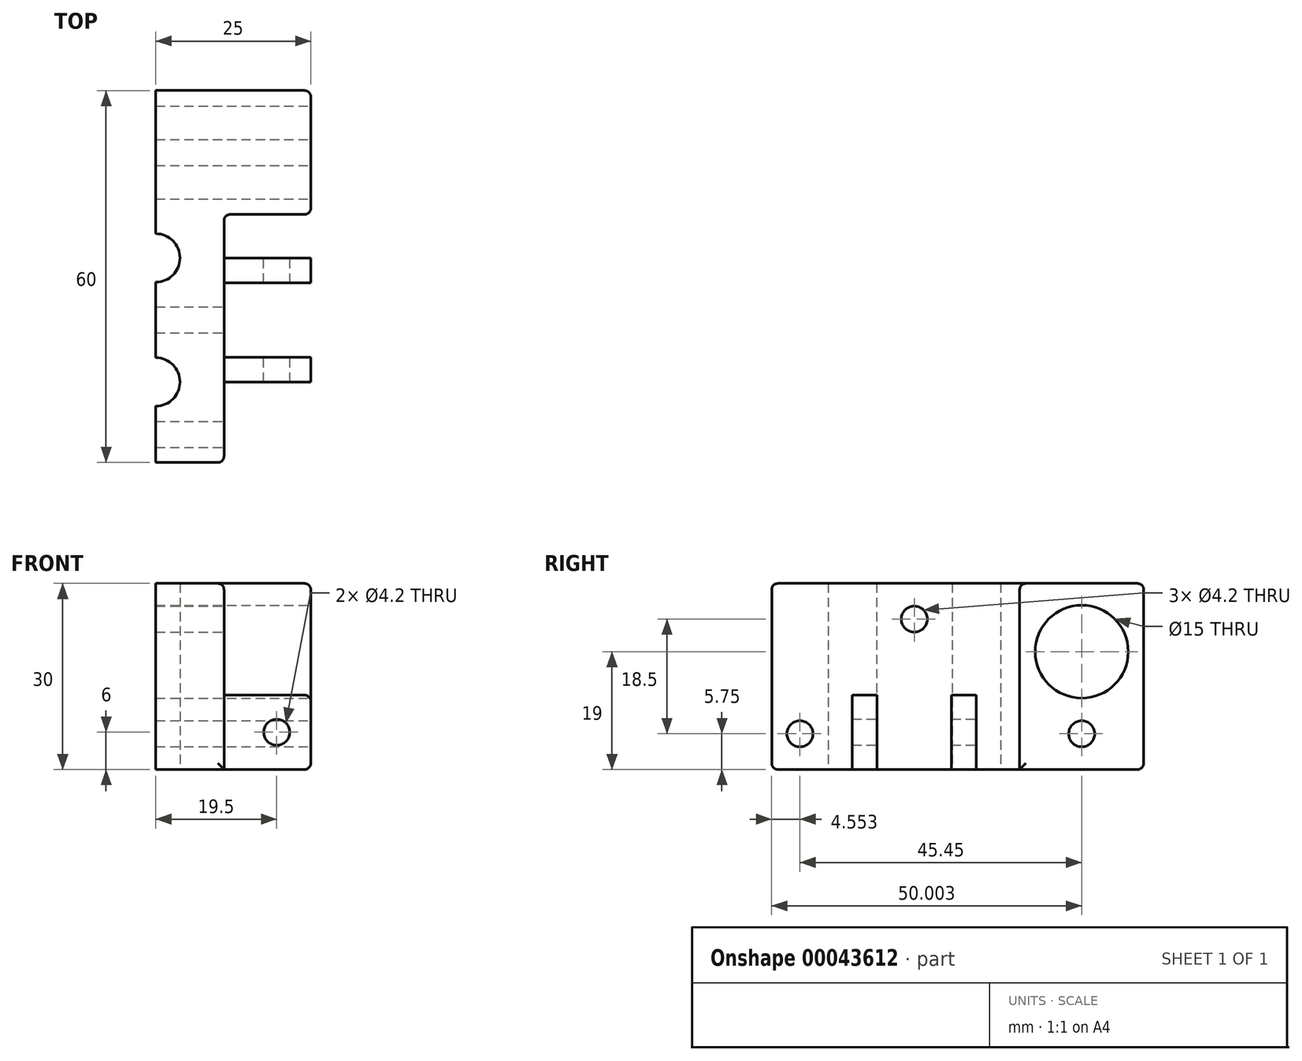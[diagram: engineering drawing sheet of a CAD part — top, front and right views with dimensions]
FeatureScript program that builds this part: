
annotation { "Feature Type Name" : "Feature", "Feature Type Description" : "" }
export const myFeature = defineFeature(function(context is Context, id is Id, definition is map)
    precondition{}
    {
        {
            var Q0;
            Q0=qCreatedBy(makeId("Top.planeOp"),FACE);
            var sketch = newSketch(context, id + "F0", { "sketchPlane" : qUnion([Q0])});
            skLineSegment(sketch, "E0.bottom", {"start": v(-39.71, 64.35) * mm, "end": v(-28.71, 64.35) * mm});
            skLineSegment(sketch, "E0.top", {"start": v(-39.71, 4.35) * mm, "end": v(-28.71, 4.35) * mm});
            skLineSegment(sketch, "E0.left", {"start": v(-39.71, 64.35) * mm, "end": v(-39.71, 4.35) * mm});
            skLineSegment(sketch, "E0.right", {"start": v(-28.71, 64.35) * mm, "end": v(-28.71, 4.35) * mm});
            skCircle(sketch, "E1", {"center": v(-39.71, 37.35) * mm, "radius": 3.9 * mm});
            skCircle(sketch, "E2", {"center": v(-39.71, 17.35) * mm, "radius": 3.9 * mm});
            skLineSegment(sketch, "E3.bottom", {"start": v(-28.71, 44.35) * mm, "end": v(-14.71, 44.35) * mm});
            skLineSegment(sketch, "E3.top", {"start": v(-28.71, 64.35) * mm, "end": v(-14.71, 64.35) * mm});
            skLineSegment(sketch, "E3.left", {"start": v(-28.71, 44.35) * mm, "end": v(-28.71, 64.35) * mm});
            skLineSegment(sketch, "E3.right", {"start": v(-14.71, 44.35) * mm, "end": v(-14.71, 64.35) * mm});
            skLineSegment(sketch, "E4.bottom", {"start": v(-28.71, 33.35) * mm, "end": v(-14.71, 33.35) * mm});
            skLineSegment(sketch, "E4.top", {"start": v(-28.71, 37.35) * mm, "end": v(-14.71, 37.35) * mm});
            skLineSegment(sketch, "E4.left", {"start": v(-28.71, 37.35) * mm, "end": v(-28.71, 33.35) * mm});
            skLineSegment(sketch, "E4.right", {"start": v(-14.71, 37.35) * mm, "end": v(-14.71, 33.35) * mm});
            skLineSegment(sketch, "E5.bottom", {"start": v(-28.71, 17.35) * mm, "end": v(-14.71, 17.35) * mm});
            skLineSegment(sketch, "E5.top", {"start": v(-28.71, 21.35) * mm, "end": v(-14.71, 21.35) * mm});
            skLineSegment(sketch, "E5.left", {"start": v(-28.71, 17.35) * mm, "end": v(-28.71, 21.35) * mm});
            skLineSegment(sketch, "E5.right", {"start": v(-14.71, 17.35) * mm, "end": v(-14.71, 21.35) * mm});
            skPoint(sketch, "E6", {"position": v(-39.71, 27.35) * mm});
            skPoint(sketch, "E7", {"position": v(-39.71, 8.9) * mm});
            skSolve(sketch);
        }
        {
            var Q0;
            {var subQ7=sQuery(id+"F0.wireOp",EDGE,"E0.bottom");Q0=makeQuery(id+"F0.imprint","IMPRINT",FACE,{"disambiguationData":[TD([[makeQuery(id+"F0.imprint","IMPRINT",EDGE,{"derivedFrom":subQ7}),-1.0]])]});}
            var Q1;
            Q1=makeQuery(id+"F0.imprint","IMPRINT",FACE,{"disambiguationData":[TD([[makeQuery(id+"F0.imprint","IMPRINT",EDGE,{"derivedFrom":sQuery(id+"F0.wireOp",EDGE,"E3.bottom")}),1.0]])]});
            extrude(context, id + "F1", {"entities" : qUnion([Q0, Q1]), "depth" : 30 * mm});
        }
        {
            var Q0;
            Q0=makeQuery(id+"F0.imprint","IMPRINT",FACE,{"disambiguationData":[TD([[makeQuery(id+"F0.imprint","IMPRINT",EDGE,{"derivedFrom":sQuery(id+"F0.wireOp",EDGE,"E4.bottom")}),1.0]])]});
            var Q1;
            Q1=makeQuery(id+"F0.imprint","IMPRINT",FACE,{"disambiguationData":[TD([[makeQuery(id+"F0.imprint","IMPRINT",EDGE,{"derivedFrom":sQuery(id+"F0.wireOp",EDGE,"E5.bottom")}),1.0]])]});
            extrude(context, id + "F2", {"entities" : qUnion([Q0, Q1]), "operationType" : NewBodyOperationType.ADD, "depth" : 12 * mm});
        }
        {
            var Q0;
            Q0=makeQuery(id+"F1.opExtrude","SWEPT_FACE",FACE,{"disambiguationData":[OSD([sQuery(id+"F0.wireOp",EDGE,"E3.right")])]});
            var sketch = newSketch(context, id + "F3", { "sketchPlane" : qUnion([Q0])});
            skCircle(sketch, "E8", {"center": v(54.35, 19) * mm, "radius": 7.5 * mm});
            skCircle(sketch, "E9", {"center": v(54.35, 5.75) * mm, "radius": 2.1 * mm});
            skCircle(sketch, "E10", {"center": v(8.9, 5.75) * mm, "radius": 2.1 * mm});
            skCircle(sketch, "E11", {"center": v(27.35, 24.25) * mm, "radius": 2.1 * mm});
            skSolve(sketch);
        }
        {
            var Q0;
            Q0=makeQuery(id+"F3.imprint","IMPRINT",FACE,{"disambiguationData":[TD([[makeQuery(id+"F3.imprint","IMPRINT",EDGE,{"derivedFrom":sQuery(id+"F3.wireOp",EDGE,"E8")}),1.0]])]});
            var Q1;
            Q1=makeQuery(id+"F3.imprint","IMPRINT",FACE,{"disambiguationData":[TD([[makeQuery(id+"F3.imprint","IMPRINT",EDGE,{"derivedFrom":sQuery(id+"F3.wireOp",EDGE,"E9")}),1.0]])]});
            var Q2;
            Q2=makeQuery(id+"F3.imprint","IMPRINT",FACE,{"disambiguationData":[TD([[makeQuery(id+"F3.imprint","IMPRINT",EDGE,{"derivedFrom":sQuery(id+"F3.wireOp",EDGE,"E11")}),1.0]])]});
            var Q3;
            Q3=makeQuery(id+"F3.imprint","IMPRINT",FACE,{"disambiguationData":[TD([[makeQuery(id+"F3.imprint","IMPRINT",EDGE,{"derivedFrom":sQuery(id+"F3.wireOp",EDGE,"E10")}),1.0]])]});
            extrude(context, id + "F4", {"entities" : qUnion([Q0, Q1, Q2, Q3]), "operationType" : NewBodyOperationType.REMOVE, "endBound" : BoundingType.THROUGH_ALL, "oppositeDirection" : true, "depth" : 25 * mm});
        }
        {
            var Q0;
            Q0=makeQuery(id+"F2.opExtrude","SWEPT_FACE",FACE,{"disambiguationData":[OSD([sQuery(id+"F0.wireOp",EDGE,"E4.top")])]});
            var sketch = newSketch(context, id + "F5", { "sketchPlane" : qUnion([Q0])});
            skCircle(sketch, "E12", {"center": v(20.21, 6) * mm, "radius": 2.1 * mm});
            skSolve(sketch);
        }
        {
            var Q0;
            Q0 = qSketchRegion(id + "F5", true);
            var Q1;
            Q1=sQuery(id+"F5.wireOp",EDGE,"E12");
            extrude(context, id + "F6", {"entities" : qUnion([Q0]), "operationType" : NewBodyOperationType.REMOVE, "surfaceEntities" : qUnion([Q1]), "oppositeDirection" : true, "depth" : 25 * mm});
        }
        {
            var Q0;
            Q0=makeQuery(id+"F2.opExtrude","CAP_EDGE",EDGE,{"disambiguationData":[OSD([sQuery(id+"F0.wireOp",EDGE,"E4.right")])],"isStart":false});
            var Q1;
            Q1=makeQuery(id+"F2.opExtrude","CAP_EDGE",EDGE,{"disambiguationData":[OSD([sQuery(id+"F0.wireOp",EDGE,"E5.right")])],"isStart":false});
            var Q2;
            Q2=makeQuery(id+"F2.opExtrude","CAP_EDGE",EDGE,{"disambiguationData":[OSD([sQuery(id+"F0.wireOp",EDGE,"E5.right")])],"isStart":true});
            var Q3;
            Q3=makeQuery(id+"F1.opExtrude","CAP_EDGE",EDGE,{"disambiguationData":[OSD([sQuery(id+"F0.wireOp",EDGE,"E3.right")])],"isStart":true});
            var Q4;
            Q4=makeQuery(id+"F1.opExtrude","SWEPT_EDGE",EDGE,{"disambiguationData":[OSD([sQuery(id+"F0.wireOp",EDGE,"E3.bottom"),sQuery(id+"F0.wireOp",EDGE,"E3.right")])]});
            var Q5;
            Q5=makeQuery(id+"F1.opExtrude","CAP_EDGE",EDGE,{"disambiguationData":[OSD([sQuery(id+"F0.wireOp",EDGE,"E3.right")])],"isStart":false});
            var Q6;
            Q6=makeQuery(id+"F1.opExtrude","SWEPT_EDGE",EDGE,{"disambiguationData":[OSD([sQuery(id+"F0.wireOp",EDGE,"E3.top"),sQuery(id+"F0.wireOp",EDGE,"E3.right")])]});
            var Q7;
            Q7=makeQuery(id+"F1.opExtrude","CAP_EDGE",EDGE,{"disambiguationData":[OSD([sQuery(id+"F0.wireOp",EDGE,"E0.bottom"),sQuery(id+"F0.wireOp",EDGE,"E3.top")])],"isStart":true});
            var Q8;
            Q8=makeQuery(id+"F1.opExtrude","CAP_EDGE",EDGE,{"disambiguationData":[OSD([sQuery(id+"F0.wireOp",EDGE,"E0.bottom"),sQuery(id+"F0.wireOp",EDGE,"E3.top")])],"isStart":false});
            var Q9;
            Q9=makeQuery(id+"F1.opExtrude","CAP_EDGE",EDGE,{"disambiguationData":[OSD([sQuery(id+"F0.wireOp",EDGE,"E0.top")])],"isStart":true});
            var Q10;
            Q10=makeQuery(id+"F1.opExtrude","SWEPT_EDGE",EDGE,{"disambiguationData":[OSD([sQuery(id+"F0.wireOp",EDGE,"E0.top"),sQuery(id+"F0.wireOp",EDGE,"E0.right")])]});
            var Q11;
            Q11=makeQuery(id+"F1.opExtrude","CAP_EDGE",EDGE,{"disambiguationData":[OSD([sQuery(id+"F0.wireOp",EDGE,"E0.right"),sQuery(id+"F0.wireOp",EDGE,"E4.left"),sQuery(id+"F0.wireOp",EDGE,"E5.left")])],"isStart":false});
            var Q12;
            Q12=makeQuery(id+"F1.opExtrude","CAP_EDGE",EDGE,{"disambiguationData":[OSD([sQuery(id+"F0.wireOp",EDGE,"E3.bottom")])],"isStart":false});
            var Q13;
            Q13=makeQuery(id+"F2.opExtrude","CAP_EDGE",EDGE,{"disambiguationData":[OSD([sQuery(id+"F0.wireOp",EDGE,"E5.left")])],"isStart":false});
            var Q14;
            Q14=makeQuery(id+"F2.opExtrude","CAP_EDGE",EDGE,{"disambiguationData":[OSD([sQuery(id+"F0.wireOp",EDGE,"E4.left")])],"isStart":false});
            var Q15;
            Q15=makeQuery(id+"F2.opExtrude","SWEPT_EDGE",EDGE,{"disambiguationData":[OSD([sQuery(id+"F0.wireOp",EDGE,"E0.right"),sQuery(id+"F0.wireOp",EDGE,"E4.top"),sQuery(id+"F0.wireOp",EDGE,"E4.left")])]});
            var Q16;
            Q16=makeQuery(id+"F2.opExtrude","SWEPT_EDGE",EDGE,{"disambiguationData":[OSD([sQuery(id+"F0.wireOp",EDGE,"E0.right"),sQuery(id+"F0.wireOp",EDGE,"E5.bottom"),sQuery(id+"F0.wireOp",EDGE,"E5.left")])]});
            var Q17;
            Q17=makeQuery(id+"F1.opExtrude","CAP_EDGE",EDGE,{"disambiguationData":[OSD([sQuery(id+"F0.wireOp",EDGE,"E0.top")])],"isStart":false});
            var Q18;
            Q18=makeQuery(id+"F1.opExtrude","SWEPT_EDGE",EDGE,{"disambiguationData":[OSD([sQuery(id+"F0.wireOp",EDGE,"E0.right"),sQuery(id+"F0.wireOp",EDGE,"E3.bottom"),sQuery(id+"F0.wireOp",EDGE,"E3.left")])]});
            var Q19;
            Q19=makeQuery(id+"F2.opExtrude","CAP_EDGE",EDGE,{"disambiguationData":[OSD([sQuery(id+"F0.wireOp",EDGE,"E4.right")])],"isStart":true});
            fillet(context, id + "F7", {"entities" : qUnion([Q0, Q1, Q2, Q3, Q4, Q5, Q6, Q7, Q8, Q9, Q10, Q11, Q12, Q13, Q14, Q15, Q16, Q17, Q18, Q19]), "radius" : 1 * mm, "tangentPropagation" : true, "allowEdgeOverflow" : false});
        }
    });
